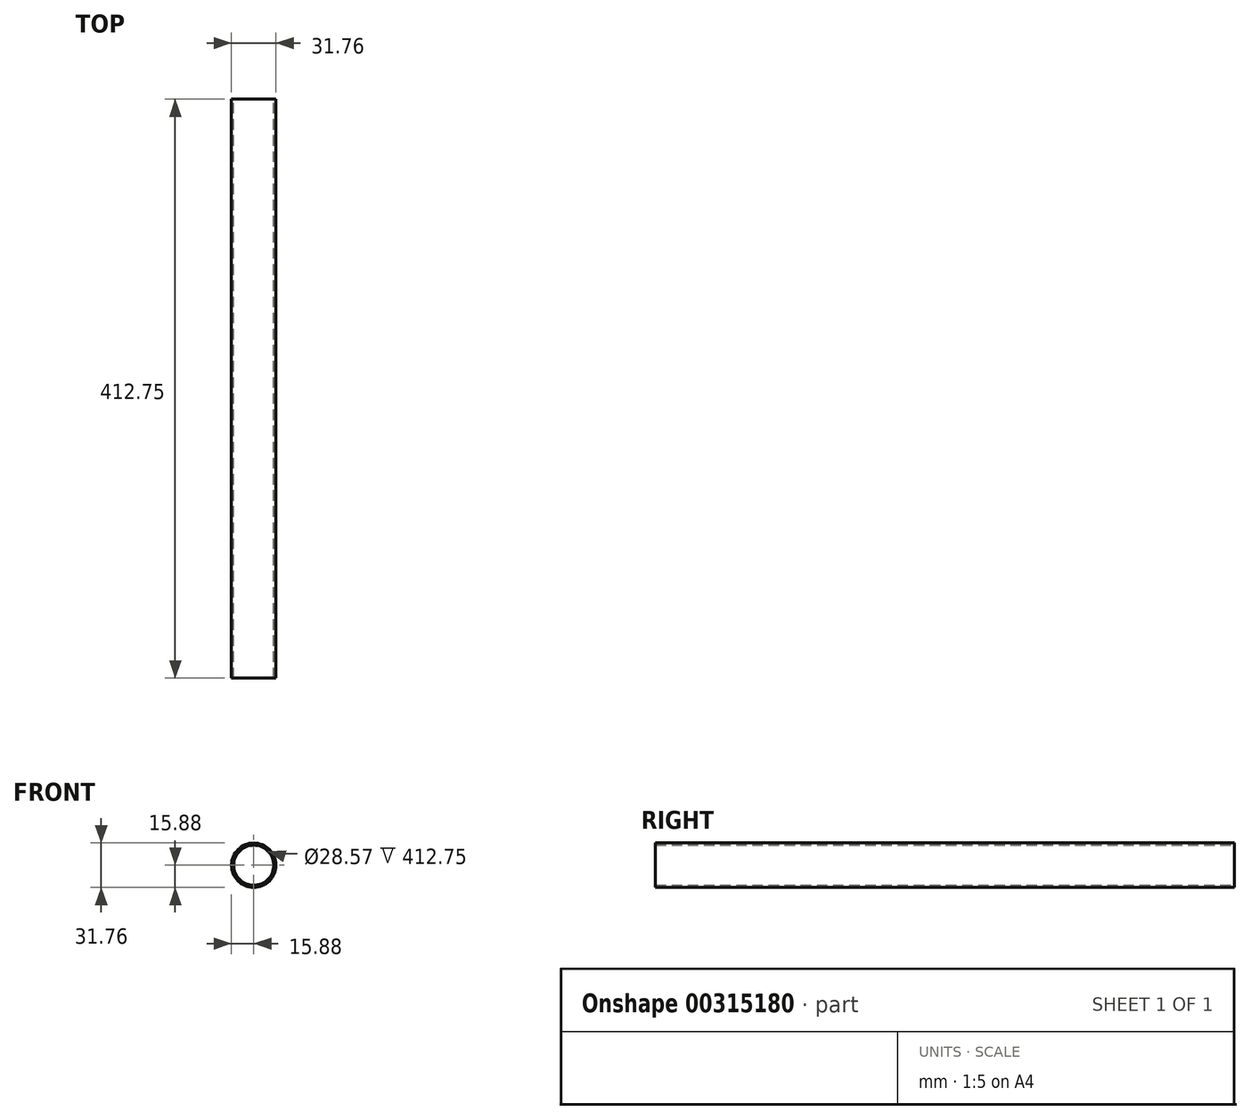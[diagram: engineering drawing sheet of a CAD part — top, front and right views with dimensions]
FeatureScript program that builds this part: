
annotation { "Feature Type Name" : "Feature", "Feature Type Description" : "" }
export const myFeature = defineFeature(function(context is Context, id is Id, definition is map)
    precondition{}
    {
        {
            var Q0;
            Q0=qCreatedBy(makeId("Front.planeOp"),FACE);
            var sketch = newSketch(context, id + "F0", { "sketchPlane" : qUnion([Q0])});
            skCircle(sketch, "E0", {"center": v(0, 0) * mm, "radius": 15.88 * mm});
            skCircle(sketch, "E1", {"center": v(0, 0) * mm, "radius": 14.29 * mm});
            skSolve(sketch);
        }
        {
            var Q0;
            Q0 = qSketchRegion(id + "F0", true);
            extrude(context, id + "F1", {"entities" : qUnion([Q0]), "depth" : 412.75 * mm});
        }
    });
